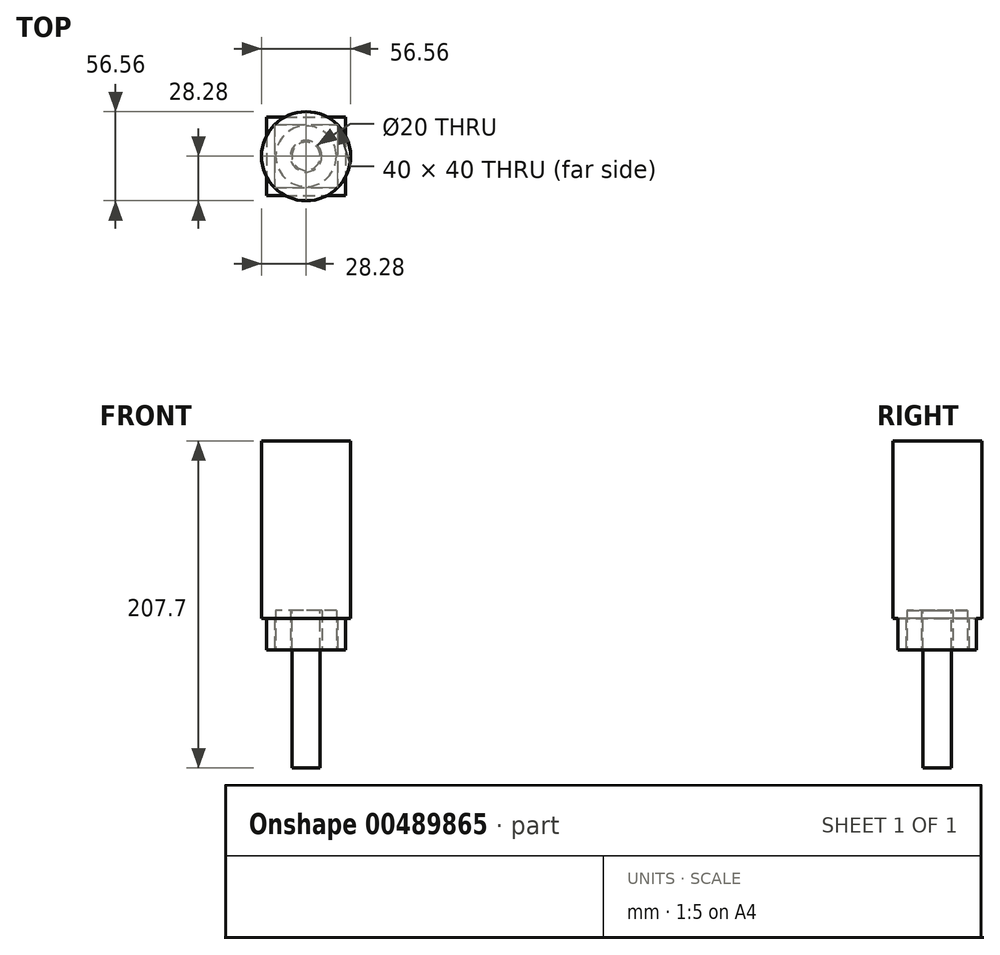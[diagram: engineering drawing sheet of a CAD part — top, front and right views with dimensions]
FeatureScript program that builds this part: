
annotation { "Feature Type Name" : "Feature", "Feature Type Description" : "" }
export const myFeature = defineFeature(function(context is Context, id is Id, definition is map)
    precondition{}
    {
        {
            var Q0;
            Q0=qCreatedBy(makeId("Top.planeOp"),FACE);
            var sketch = newSketch(context, id + "F0", { "sketchPlane" : qUnion([Q0])});
            skLineSegment(sketch, "E0.bottom", {"start": v(-20, 20) * mm, "end": v(20, 20) * mm});
            skLineSegment(sketch, "E0.top", {"start": v(-20, -20) * mm, "end": v(20, -20) * mm});
            skLineSegment(sketch, "E0.left", {"start": v(-20, 20) * mm, "end": v(-20, -20) * mm});
            skLineSegment(sketch, "E0.right", {"start": v(20, 20) * mm, "end": v(20, -20) * mm});
            skPoint(sketch, "E0.middle", {"position": v(0, 0) * mm});
            skLineSegment(sketch, "E1.bottom", {"start": v(-25, 25) * mm, "end": v(25, 25) * mm});
            skLineSegment(sketch, "E1.top", {"start": v(-25, -25) * mm, "end": v(25, -25) * mm});
            skLineSegment(sketch, "E1.left", {"start": v(-25, 25) * mm, "end": v(-25, -25) * mm});
            skLineSegment(sketch, "E1.right", {"start": v(25, 25) * mm, "end": v(25, -25) * mm});
            skCircle(sketch, "E2", {"center": v(0, 0) * mm, "radius": 19.25 * mm});
            skCircle(sketch, "E3", {"center": v(0, 0) * mm, "radius": 10 * mm});
            skSolve(sketch);
        }
        {
            var Q0;
            Q0=makeQuery(id+"F0.imprint","IMPRINT",FACE,{"disambiguationData":[TD([[makeQuery(id+"F0.imprint","IMPRINT",EDGE,{"derivedFrom":sQuery(id+"F0.wireOp",EDGE,"E2")}),1.0]])]});
            extrude(context, id + "F1", {"entities" : qUnion([Q0]), "depth" : 25 * mm});
        }
        {
            var Q0;
            Q0 = qSketchRegion(id + "F0", true);
            extrude(context, id + "F2", {"entities" : qUnion([Q0]), "depth" : 20 * mm});
        }
        {
            var Q0;
            Q0=makeQuery(id+"F1.opExtrude","CAP_FACE",FACE,{"disambiguationData":[OSD([sQuery(id+"F0.wireOp",EDGE,"E2"),sQuery(id+"F0.wireOp",EDGE,"E3")])],"isStart":false});
            var sketch = newSketch(context, id + "F3", { "sketchPlane" : qUnion([Q0])});
            skCircle(sketch, "E4", {"center": v(0, 0) * mm, "radius": 9 * mm});
            skSolve(sketch);
        }
        {
            var Q0;
            Q0=makeQuery(id+"F3.imprint","IMPRINT",FACE,{"disambiguationData":[TD([[makeQuery(id+"F3.imprint","IMPRINT",EDGE,{"derivedFrom":sQuery(id+"F3.wireOp",EDGE,"E4")}),1.0]])]});
            extrude(context, id + "F4", {"entities" : qUnion([Q0]), "oppositeDirection" : true, "depth" : 100 * mm});
        }
        {
            var Q0;
            Q0=makeQuery(id+"F2.opExtrude","CAP_FACE",FACE,{"disambiguationData":[OSD([sQuery(id+"F0.wireOp",EDGE,"E0.bottom"),sQuery(id+"F0.wireOp",EDGE,"E0.top"),sQuery(id+"F0.wireOp",EDGE,"E0.left"),sQuery(id+"F0.wireOp",EDGE,"E0.right"),sQuery(id+"F0.wireOp",EDGE,"E1.bottom"),sQuery(id+"F0.wireOp",EDGE,"E1.top"),sQuery(id+"F0.wireOp",EDGE,"E1.left"),sQuery(id+"F0.wireOp",EDGE,"E1.right")])],"isStart":false});
            var sketch = newSketch(context, id + "F5", { "sketchPlane" : qUnion([Q0])});
            skCircle(sketch, "E5", {"center": v(0, 0) * mm, "radius": 28.28 * mm});
            skSolve(sketch);
        }
        {
            var Q0;
            Q0=makeQuery(id+"F5.imprint","IMPRINT",FACE,{"disambiguationData":[TD([[makeQuery(id+"F5.imprint","IMPRINT",EDGE,{"derivedFrom":makeQuery(id+"F2.opExtrude","CAP_EDGE",EDGE,{"disambiguationData":[OSD([sQuery(id+"F0.wireOp",EDGE,"E0.bottom")])],"isStart":false})}),-1.0]])]});
            var Q1;
            {var subQ1=makeQuery(id+"F2.opExtrude","CAP_EDGE",EDGE,{"disambiguationData":[OSD([sQuery(id+"F0.wireOp",EDGE,"E0.right")])],"isStart":false});Q1=makeQuery(id+"F5.imprint","IMPRINT",FACE,{"disambiguationData":[TD([[makeQuery(id+"F5.imprint","IMPRINT",EDGE,{"derivedFrom":subQ1}),1.0]])]});}
            var Q2;
            {var subQ1=makeQuery(id+"F2.opExtrude","CAP_EDGE",EDGE,{"disambiguationData":[OSD([sQuery(id+"F0.wireOp",EDGE,"E0.bottom")])],"isStart":false});Q2=makeQuery(id+"F5.imprint","IMPRINT",FACE,{"disambiguationData":[TD([[makeQuery(id+"F5.imprint","IMPRINT",EDGE,{"derivedFrom":subQ1}),1.0]])]});}
            var Q3;
            {var subQ0=sQuery(id+"F5.wireOp",EDGE,"E5");var subQ1=makeQuery(id+"F2.opExtrude","CAP_EDGE",EDGE,{"disambiguationData":[OSD([sQuery(id+"F0.wireOp",EDGE,"E1.bottom")])],"isStart":false});var subQ2=makeQuery(id+"F5.imprint","INTERSECT",VERTEX,{"disambiguationData":[OD(0.0)],"derivedFrom":[subQ1,subQ0]});Q3=makeQuery(id+"F5.imprint","IMPRINT",FACE,{"disambiguationData":[TD([[makeQuery(id+"F5.imprint","IMPRINT",EDGE,{"disambiguationData":[TD([[subQ2,-1.0]])],"derivedFrom":subQ0}),1.0]])]});}
            var Q4;
            {var subQ1=makeQuery(id+"F2.opExtrude","CAP_EDGE",EDGE,{"disambiguationData":[OSD([sQuery(id+"F0.wireOp",EDGE,"E0.left")])],"isStart":false});Q4=makeQuery(id+"F5.imprint","IMPRINT",FACE,{"disambiguationData":[TD([[makeQuery(id+"F5.imprint","IMPRINT",EDGE,{"derivedFrom":subQ1}),-1.0]])]});}
            var Q5;
            {var subQ0=sQuery(id+"F5.wireOp",EDGE,"E5");var subQ1=makeQuery(id+"F2.opExtrude","CAP_EDGE",EDGE,{"disambiguationData":[OSD([sQuery(id+"F0.wireOp",EDGE,"E1.left")])],"isStart":false});var subQ2=makeQuery(id+"F5.imprint","INTERSECT",VERTEX,{"disambiguationData":[OD(0.0)],"derivedFrom":[subQ1,subQ0]});Q5=makeQuery(id+"F5.imprint","IMPRINT",FACE,{"disambiguationData":[TD([[makeQuery(id+"F5.imprint","IMPRINT",EDGE,{"disambiguationData":[TD([[subQ2,-1.0]])],"derivedFrom":subQ0}),1.0]])]});}
            var Q6;
            {var subQ0=sQuery(id+"F5.wireOp",EDGE,"E5");var subQ1=makeQuery(id+"F2.opExtrude","CAP_EDGE",EDGE,{"disambiguationData":[OSD([sQuery(id+"F0.wireOp",EDGE,"E1.top")])],"isStart":false});var subQ2=makeQuery(id+"F5.imprint","INTERSECT",VERTEX,{"disambiguationData":[OD(0.0)],"derivedFrom":[subQ1,subQ0]});Q6=makeQuery(id+"F5.imprint","IMPRINT",FACE,{"disambiguationData":[TD([[makeQuery(id+"F5.imprint","IMPRINT",EDGE,{"disambiguationData":[TD([[subQ2,-1.0]])],"derivedFrom":subQ0}),1.0]])]});}
            var Q7;
            {var subQ1=makeQuery(id+"F2.opExtrude","CAP_EDGE",EDGE,{"disambiguationData":[OSD([sQuery(id+"F0.wireOp",EDGE,"E0.top")])],"isStart":false});Q7=makeQuery(id+"F5.imprint","IMPRINT",FACE,{"disambiguationData":[TD([[makeQuery(id+"F5.imprint","IMPRINT",EDGE,{"derivedFrom":subQ1}),-1.0]])]});}
            var Q8;
            {var subQ0=sQuery(id+"F5.wireOp",EDGE,"E5");var subQ1=makeQuery(id+"F2.opExtrude","CAP_EDGE",EDGE,{"disambiguationData":[OSD([sQuery(id+"F0.wireOp",EDGE,"E1.right")])],"isStart":false});var subQ2=makeQuery(id+"F5.imprint","INTERSECT",VERTEX,{"disambiguationData":[OD(0.0)],"derivedFrom":[subQ1,subQ0]});Q8=makeQuery(id+"F5.imprint","IMPRINT",FACE,{"disambiguationData":[TD([[makeQuery(id+"F5.imprint","IMPRINT",EDGE,{"disambiguationData":[TD([[subQ2,1.0]])],"derivedFrom":subQ0}),1.0]])]});}
            extrude(context, id + "F6", {"entities" : qUnion([Q0, Q1, Q2, Q3, Q4, Q5, Q6, Q7, Q8]), "depth" : 112.7 * mm});
        }
    });
